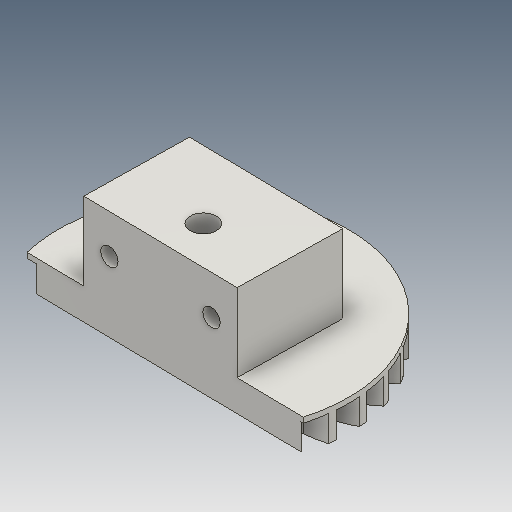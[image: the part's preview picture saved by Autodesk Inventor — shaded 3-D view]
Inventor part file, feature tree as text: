
AUTODESK INVENTOR PART (.ipt)
format: ipt  version: 2018 (Build 220112000, 112)  size: 296,448 bytes
history: native  units: mm
features: other x13, sketch x9, plane x4
ambient origin geometry x8: Origin, YZ Plane, XZ Plane, XY Plane, X Axis, Y Axis, Z Axis, Center Point
bodies: Volumenkörper1 (feature_tree)
feature tree (26):
  other  "Stirnzahnrad11_MIR.ipt"
  other  "Volumenkörper1::Stirnzahnrad11_MIR.ipt"
  other  "Bezeichnung1"
  sketch  "Sketch1"  dims[d0=10.0mm]
  sketch  "Sketch2"  dims[d16=40.0mm d17=0.0mm d41=0.0mm d43=40.0mm d46=40.0mm d47=0.0mm d48=0.0mm]
  sketch  "Skizze9"
  sketch  "Skizze10"
  sketch  "Skizze11"
  sketch  "Skizze12"
  sketch  "Skizze13"
  sketch  "Skizze14"
  sketch  "Skizze15"
  plane  "XZ Plane_1"
  plane  "Work Plane2"
  plane  "Work Plane8"
  plane  "Work Plane9"
  other  "Z Axis_1"
  other  "Flä1"
  other  "Flä1::Abgeleitet"
  other  "Abstands-iMate"
  other  "Ausrichtungs-iMate"
  other  "Netz-iMate"
  other  "Achsen-iMate"
  other  "Positions-iMate"
  other  "Netz-iMate 2"
  other  "Startebenen-iMate"
